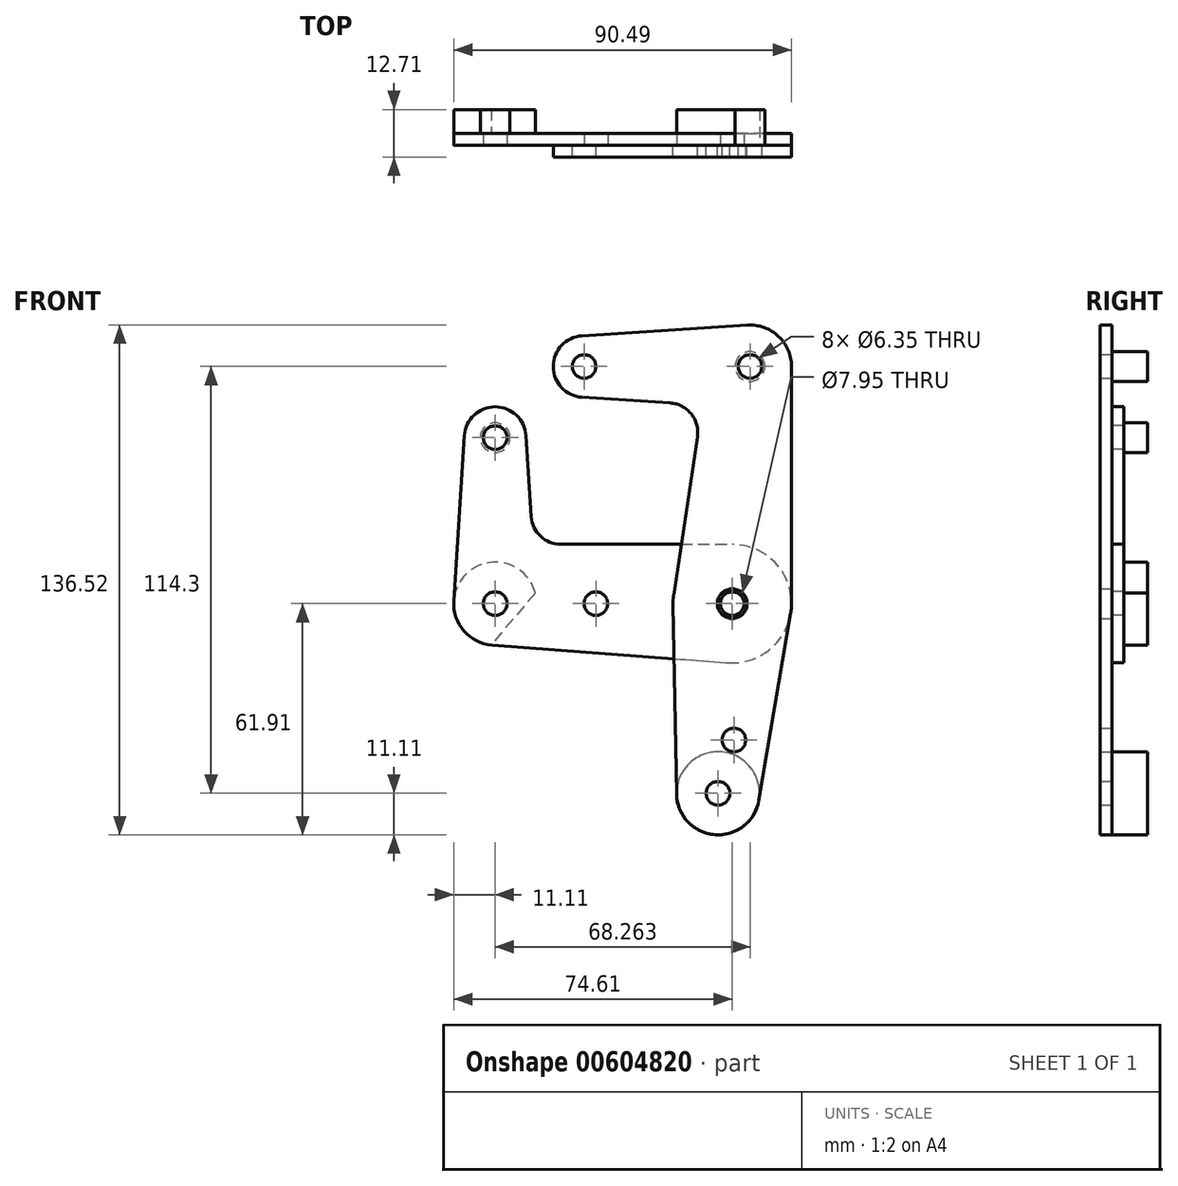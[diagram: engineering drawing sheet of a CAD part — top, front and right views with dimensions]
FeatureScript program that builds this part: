
annotation { "Feature Type Name" : "Feature", "Feature Type Description" : "" }
export const myFeature = defineFeature(function(context is Context, id is Id, definition is map)
    precondition{}
    {
        {
            var Q0;
            Q0=qCreatedBy(makeId("Front.planeOp"),FACE);
            var sketch = newSketch(context, id + "F0", { "sketchPlane" : qUnion([Q0])});
            skCircle(sketch, "E0", {"center": v(-39.69, 63.5) * mm, "radius": 8.26 * mm});
            skCircle(sketch, "E1", {"center": v(4.76, 63.5) * mm, "radius": 11.11 * mm});
            skCircle(sketch, "E2", {"center": v(0, 0) * mm, "radius": 15.88 * mm});
            skCircle(sketch, "E3", {"center": v(-3.8, -50.8) * mm, "radius": 11.11 * mm});
            skLineSegment(sketch, "E4", {"start": v(4.76, 63.5) * mm, "end": v(-39.69, 63.5) * mm, "construction": true});
            skCircle(sketch, "E5", {"center": v(-39.69, 63.5) * mm, "radius": 3.18 * mm});
            skCircle(sketch, "E6", {"center": v(4.76, 63.5) * mm, "radius": 3.18 * mm});
            skCircle(sketch, "E7", {"center": v(0, 0) * mm, "radius": 3.18 * mm});
            skCircle(sketch, "E8", {"center": v(-3.8, -50.8) * mm, "radius": 3.18 * mm});
            skCircle(sketch, "E9", {"center": v(0.44, -36.52) * mm, "radius": 3.18 * mm});
            skCircle(sketch, "E10", {"center": v(0, 0) * mm, "radius": 3.98 * mm});
            skLineSegment(sketch, "E11", {"start": v(-15.87, -0.3) * mm, "end": v(-14.92, -51) * mm});
            skLineSegment(sketch, "E12", {"start": v(15.65, -2.66) * mm, "end": v(7.15, -52.66) * mm});
            skLineSegment(sketch, "E13", {"start": v(-40.22, 71.74) * mm, "end": v(4.05, 74.59) * mm});
            skLineSegment(sketch, "E14", {"start": v(-40.22, 55.26) * mm, "end": v(-16.67, 53.75) * mm});
            skLineSegment(sketch, "E15", {"start": v(-9.32, 44.63) * mm, "end": v(-15.7, 2.37) * mm});
            skLineSegment(sketch, "E16", {"start": v(15.87, 63.5) * mm, "end": v(15.87, 0) * mm});
            skArc(sketch, "E17.filletArc", {"start": v(-9.32, 44.63) * mm, "mid": v(-11, 50.8) * mm, "end": v(-16.67, 53.75) * mm});
            skLineSegment(sketch, "E18", {"start": v(-39.69, 63.5) * mm, "end": v(-63.5, 44.45) * mm, "construction": true});
            skLineSegment(sketch, "E19", {"start": v(-63.5, 44.45) * mm, "end": v(-63.5, 0) * mm, "construction": true});
            skLineSegment(sketch, "E20", {"start": v(0, 0) * mm, "end": v(-63.5, 0) * mm, "construction": true});
            skCircle(sketch, "E21", {"center": v(-63.5, 44.45) * mm, "radius": 8.26 * mm});
            skCircle(sketch, "E22", {"center": v(-63.5, 44.45) * mm, "radius": 3.18 * mm});
            skCircle(sketch, "E23", {"center": v(-63.5, 0) * mm, "radius": 11.11 * mm});
            skCircle(sketch, "E24", {"center": v(-63.5, 0) * mm, "radius": 3.18 * mm});
            skLineSegment(sketch, "E25", {"start": v(-55.26, 44.98) * mm, "end": v(-53.87, 23.31) * mm});
            skLineSegment(sketch, "E26", {"start": v(-71.74, 44.98) * mm, "end": v(-74.59, 0.71) * mm});
            skLineSegment(sketch, "E27", {"start": v(-45.93, 15.88) * mm, "end": v(0, 15.88) * mm});
            skLineSegment(sketch, "E28", {"start": v(-64.33, -11.08) * mm, "end": v(-1.2, -15.83) * mm});
            skLineSegment(sketch, "E29", {"start": v(4.76, 63.5) * mm, "end": v(-3.8, -50.8) * mm, "construction": true});
            skArc(sketch, "E30.filletArc", {"start": v(-53.87, 23.31) * mm, "mid": v(-51.37, 18.03) * mm, "end": v(-45.93, 15.88) * mm});
            skCircle(sketch, "E31", {"center": v(-36.53, 0) * mm, "radius": 3.18 * mm});
            skLineSegment(sketch, "E32", {"start": v(-63.5, 0) * mm, "end": v(-3.8, -50.8) * mm, "construction": true});
            skLineSegment(sketch, "E33", {"start": v(-52.75, 2.83) * mm, "end": v(-64.6, -11.08) * mm});
            skSolve(sketch);
        }
        {
            var Q0;
            {var subQ5=sQuery(id+"F0.wireOp",EDGE,"E13");Q0=makeQuery(id+"F0.imprint","IMPRINT",FACE,{"disambiguationData":[TD([[makeQuery(id+"F0.imprint","IMPRINT",EDGE,{"derivedFrom":subQ5}),-1.0]])]});}
            var Q1;
            Q1=makeQuery(id+"F0.imprint","IMPRINT",FACE,{"disambiguationData":[TD([[makeQuery(id+"F0.imprint","IMPRINT",EDGE,{"derivedFrom":sQuery(id+"F0.wireOp",EDGE,"E6")}),-1.0]])]});
            var Q2;
            Q2=makeQuery(id+"F0.imprint","IMPRINT",FACE,{"disambiguationData":[TD([[makeQuery(id+"F0.imprint","IMPRINT",EDGE,{"derivedFrom":sQuery(id+"F0.wireOp",EDGE,"E5")}),-1.0]])]});
            var Q3;
            Q3=makeQuery(id+"F0.imprint","IMPRINT",FACE,{"disambiguationData":[TD([[makeQuery(id+"F0.imprint","IMPRINT",EDGE,{"derivedFrom":sQuery(id+"F0.wireOp",EDGE,"E10")}),-1.0]])]});
            var Q4;
            {var subQ0=sQuery(id+"F0.wireOp",EDGE,"E15");var subQ1=sQuery(id+"F0.wireOp",EDGE,"E2");var subQ2=makeQuery(id+"F0.imprint","INTERSECT",VERTEX,{"derivedFrom":[subQ1,subQ0]});Q4=makeQuery(id+"F0.imprint","IMPRINT",FACE,{"disambiguationData":[TD([[makeQuery(id+"F0.imprint","IMPRINT",EDGE,{"disambiguationData":[TD([[subQ2,1.0]])],"derivedFrom":subQ1}),-1.0]])]});}
            var Q5;
            {var subQ0=sQuery(id+"F0.wireOp",EDGE,"E11");var subQ1=sQuery(id+"F0.wireOp",EDGE,"E2");var subQ2=makeQuery(id+"F0.imprint","INTERSECT",VERTEX,{"derivedFrom":[subQ1,subQ0]});Q5=makeQuery(id+"F0.imprint","IMPRINT",FACE,{"disambiguationData":[TD([[makeQuery(id+"F0.imprint","IMPRINT",EDGE,{"disambiguationData":[TD([[subQ2,-1.0]])],"derivedFrom":subQ1}),-1.0]])]});}
            var Q6;
            Q6=makeQuery(id+"F0.imprint","IMPRINT",FACE,{"disambiguationData":[TD([[makeQuery(id+"F0.imprint","IMPRINT",EDGE,{"derivedFrom":sQuery(id+"F0.wireOp",EDGE,"E9")}),-1.0]])]});
            var Q7;
            Q7=makeQuery(id+"F0.imprint","IMPRINT",FACE,{"disambiguationData":[TD([[makeQuery(id+"F0.imprint","IMPRINT",EDGE,{"derivedFrom":sQuery(id+"F0.wireOp",EDGE,"E8")}),-1.0]])]});
            extrude(context, id + "F1", {"entities" : qUnion([Q0, Q1, Q2, Q3, Q4, Q5, Q6, Q7]), "depth" : 3.17 * mm, "offsetDistance" : 25.4 * mm});
        }
        {
            var Q0;
            Q0=makeQuery(id+"F0.imprint","IMPRINT",FACE,{"disambiguationData":[TD([[makeQuery(id+"F0.imprint","IMPRINT",EDGE,{"derivedFrom":sQuery(id+"F0.wireOp",EDGE,"E22")}),-1.0]])]});
            var Q1;
            {var subQ6=sQuery(id+"F0.wireOp",EDGE,"E25");Q1=makeQuery(id+"F0.imprint","IMPRINT",FACE,{"disambiguationData":[TD([[makeQuery(id+"F0.imprint","IMPRINT",EDGE,{"derivedFrom":subQ6}),-1.0]])]});}
            var Q2;
            {var subQ0=sQuery(id+"F0.wireOp",EDGE,"E11");var subQ1=sQuery(id+"F0.wireOp",EDGE,"E2");var subQ2=makeQuery(id+"F0.imprint","INTERSECT",VERTEX,{"derivedFrom":[subQ1,subQ0]});Q2=makeQuery(id+"F0.imprint","IMPRINT",FACE,{"disambiguationData":[TD([[makeQuery(id+"F0.imprint","IMPRINT",EDGE,{"disambiguationData":[TD([[subQ2,-1.0]])],"derivedFrom":subQ1}),-1.0]])]});}
            var Q3;
            {var subQ0=sQuery(id+"F0.wireOp",EDGE,"E15");var subQ1=sQuery(id+"F0.wireOp",EDGE,"E2");var subQ2=makeQuery(id+"F0.imprint","INTERSECT",VERTEX,{"derivedFrom":[subQ1,subQ0]});Q3=makeQuery(id+"F0.imprint","IMPRINT",FACE,{"disambiguationData":[TD([[makeQuery(id+"F0.imprint","IMPRINT",EDGE,{"disambiguationData":[TD([[subQ2,1.0]])],"derivedFrom":subQ1}),-1.0]])]});}
            var Q4;
            Q4=makeQuery(id+"F0.imprint","IMPRINT",FACE,{"disambiguationData":[TD([[makeQuery(id+"F0.imprint","IMPRINT",EDGE,{"derivedFrom":sQuery(id+"F0.wireOp",EDGE,"E10")}),-1.0]])]});
            var Q5;
            Q5=makeQuery(id+"F0.imprint","IMPRINT",FACE,{"disambiguationData":[TD([[makeQuery(id+"F0.imprint","IMPRINT",EDGE,{"derivedFrom":sQuery(id+"F0.wireOp",EDGE,"E7")}),-1.0]])]});
            var Q6;
            {var subQ0=sQuery(id+"F0.wireOp",EDGE,"E23");var subQ1=makeQuery(id+"F0.imprint","INTERSECT",VERTEX,{"derivedFrom":[subQ0,sQuery(id+"F0.wireOp",EDGE,"E28")]});Q6=makeQuery(id+"F0.imprint","IMPRINT",FACE,{"disambiguationData":[TD([[makeQuery(id+"F0.imprint","IMPRINT",EDGE,{"disambiguationData":[TD([[subQ1,1.0]])],"derivedFrom":subQ0}),1.0]])]});}
            var Q7;
            Q7=makeQuery(id+"F0.imprint","IMPRINT",FACE,{"disambiguationData":[TD([[makeQuery(id+"F0.imprint","IMPRINT",EDGE,{"derivedFrom":sQuery(id+"F0.wireOp",EDGE,"E24")}),-1.0]])]});
            extrude(context, id + "F2", {"entities" : qUnion([Q0, Q1, Q2, Q3, Q4, Q5, Q6, Q7]), "oppositeDirection" : true, "depth" : 3.17 * mm, "offsetDistance" : 25.4 * mm});
        }
        {
            var Q0;
            Q0=makeQuery(id+"F1.opExtrude","CAP_FACE",FACE,{"disambiguationData":[OSD([sQuery(id+"F0.wireOp",EDGE,"E0"),sQuery(id+"F0.wireOp",EDGE,"E1"),sQuery(id+"F0.wireOp",EDGE,"E2"),sQuery(id+"F0.wireOp",EDGE,"E3"),sQuery(id+"F0.wireOp",EDGE,"E5"),sQuery(id+"F0.wireOp",EDGE,"E6"),sQuery(id+"F0.wireOp",EDGE,"E7"),sQuery(id+"F0.wireOp",EDGE,"E8"),sQuery(id+"F0.wireOp",EDGE,"E9"),sQuery(id+"F0.wireOp",EDGE,"E11"),sQuery(id+"F0.wireOp",EDGE,"E12"),sQuery(id+"F0.wireOp",EDGE,"E13"),sQuery(id+"F0.wireOp",EDGE,"E14"),sQuery(id+"F0.wireOp",EDGE,"E15"),sQuery(id+"F0.wireOp",EDGE,"E16"),sQuery(id+"F0.wireOp",EDGE,"E17.filletArc")])],"isStart":false});
            var sketch = newSketch(context, id + "F3", { "sketchPlane" : qUnion([Q0])});
            skCircle(sketch, "E34.0", {"center": v(-3.8, -50.8) * mm, "radius": 11.11 * mm});
            skCircle(sketch, "E35", {"center": v(4.76, 63.5) * mm, "radius": 3.98 * mm});
            skSolve(sketch);
        }
        {
            var Q0;
            Q0=makeQuery(id+"F0.imprint","IMPRINT",FACE,{"disambiguationData":[TD([[makeQuery(id+"F0.imprint","IMPRINT",EDGE,{"derivedFrom":sQuery(id+"F0.wireOp",EDGE,"E22")}),-1.0]])]});
            var sketch = newSketch(context, id + "F4", { "sketchPlane" : qUnion([Q0])});
            skCircle(sketch, "E36", {"center": v(-63.5, 44.45) * mm, "radius": 3.98 * mm});
            skLineSegment(sketch, "E37.0.0", {"start": v(-64.57, -11.06) * mm, "end": v(-52.75, 2.83) * mm});
            skArc(sketch, "E37.0.1", {"start": v(-52.75, 2.83) * mm, "mid": v(-64.57, 11.06) * mm, "end": v(-74.59, 0.71) * mm});
            skArc(sketch, "E37.0.2", {"start": v(-74.59, 0.71) * mm, "mid": v(-71.96, -7.2) * mm, "end": v(-64.57, -11.06) * mm});
            skSolve(sketch);
        }
        {
            var Q0;
            Q0=qCreatedBy(makeId("Front.planeOp"),FACE);
            cPlane(context, id + "F5", {"entities" : qUnion([Q0]), "cplaneType" : CPlaneType.OFFSET, "offset" : 9.52 * mm, "oppositeDirection" : true, "width" : 152.4 * mm, "height" : 152.4 * mm});
        }
        {
            var Q0;
            Q0 = qSketchRegion(id + "F3", true);
            var Q1;
            Q1 = qSketchRegion(id + "F4", true);
            var Q2;
            Q2=qCreatedBy(id+"F5.planeOp",FACE);
            extrude(context, id + "F6", {"entities" : qUnion([Q0, Q1]), "endBound" : BoundingType.UP_TO_SURFACE, "oppositeDirection" : true, "depth" : 25.4 * mm, "endBoundEntityFace" : qUnion([Q2]), "offsetDistance" : 25.4 * mm});
        }
        {
            var Q0;
            Q0=makeQuery(id+"F1.opExtrude","SWEPT_BODY",BODY,{"disambiguationData":[OSD([sQuery(id+"F0.wireOp",EDGE,"E0"),sQuery(id+"F0.wireOp",EDGE,"E1"),sQuery(id+"F0.wireOp",EDGE,"E2"),sQuery(id+"F0.wireOp",EDGE,"E3"),sQuery(id+"F0.wireOp",EDGE,"E5"),sQuery(id+"F0.wireOp",EDGE,"E6"),sQuery(id+"F0.wireOp",EDGE,"E7"),sQuery(id+"F0.wireOp",EDGE,"E8"),sQuery(id+"F0.wireOp",EDGE,"E9"),sQuery(id+"F0.wireOp",EDGE,"E11"),sQuery(id+"F0.wireOp",EDGE,"E12"),sQuery(id+"F0.wireOp",EDGE,"E13"),sQuery(id+"F0.wireOp",EDGE,"E14"),sQuery(id+"F0.wireOp",EDGE,"E15"),sQuery(id+"F0.wireOp",EDGE,"E16"),sQuery(id+"F0.wireOp",EDGE,"E17.filletArc")])]});
            var Q1;
            Q1=makeQuery(id+"F2.opExtrude","SWEPT_BODY",BODY,{"disambiguationData":[OSD([sQuery(id+"F0.wireOp",EDGE,"E2"),sQuery(id+"F0.wireOp",EDGE,"E7"),sQuery(id+"F0.wireOp",EDGE,"E21"),sQuery(id+"F0.wireOp",EDGE,"E22"),sQuery(id+"F0.wireOp",EDGE,"E23"),sQuery(id+"F0.wireOp",EDGE,"E24"),sQuery(id+"F0.wireOp",EDGE,"E25"),sQuery(id+"F0.wireOp",EDGE,"E26"),sQuery(id+"F0.wireOp",EDGE,"E27"),sQuery(id+"F0.wireOp",EDGE,"E28"),sQuery(id+"F0.wireOp",EDGE,"E30.filletArc"),sQuery(id+"F0.wireOp",EDGE,"E31")])]});
            var Q2;
            Q2=makeQuery(id+"F6.opExtrude","SWEPT_BODY",BODY,{"disambiguationData":[OSD([sQuery(id+"F3.wireOp",EDGE,"E34.0")])]});
            var Q3;
            Q3=makeQuery(id+"F6.opExtrude","SWEPT_BODY",BODY,{"disambiguationData":[OSD([sQuery(id+"F4.wireOp",EDGE,"E37.0.0"),sQuery(id+"F4.wireOp",EDGE,"E37.0.1"),sQuery(id+"F4.wireOp",EDGE,"E37.0.2")])]});
            var Q4;
            Q4=makeQuery(id+"F6.opExtrude","SWEPT_BODY",BODY,{"disambiguationData":[OSD([sQuery(id+"F4.wireOp",EDGE,"E36")])]});
            var Q5;
            Q5=makeQuery(id+"F6.opExtrude","SWEPT_BODY",BODY,{"disambiguationData":[OSD([sQuery(id+"F3.wireOp",EDGE,"E35")])]});
            booleanBodies(context, id + "F7", {"operationType" : BooleanOperationType.SUBTRACTION, "tools" : qUnion([Q0, Q1]), "targets" : qUnion([Q2, Q3, Q4, Q5]), "keepTools" : true});
        }
    });
